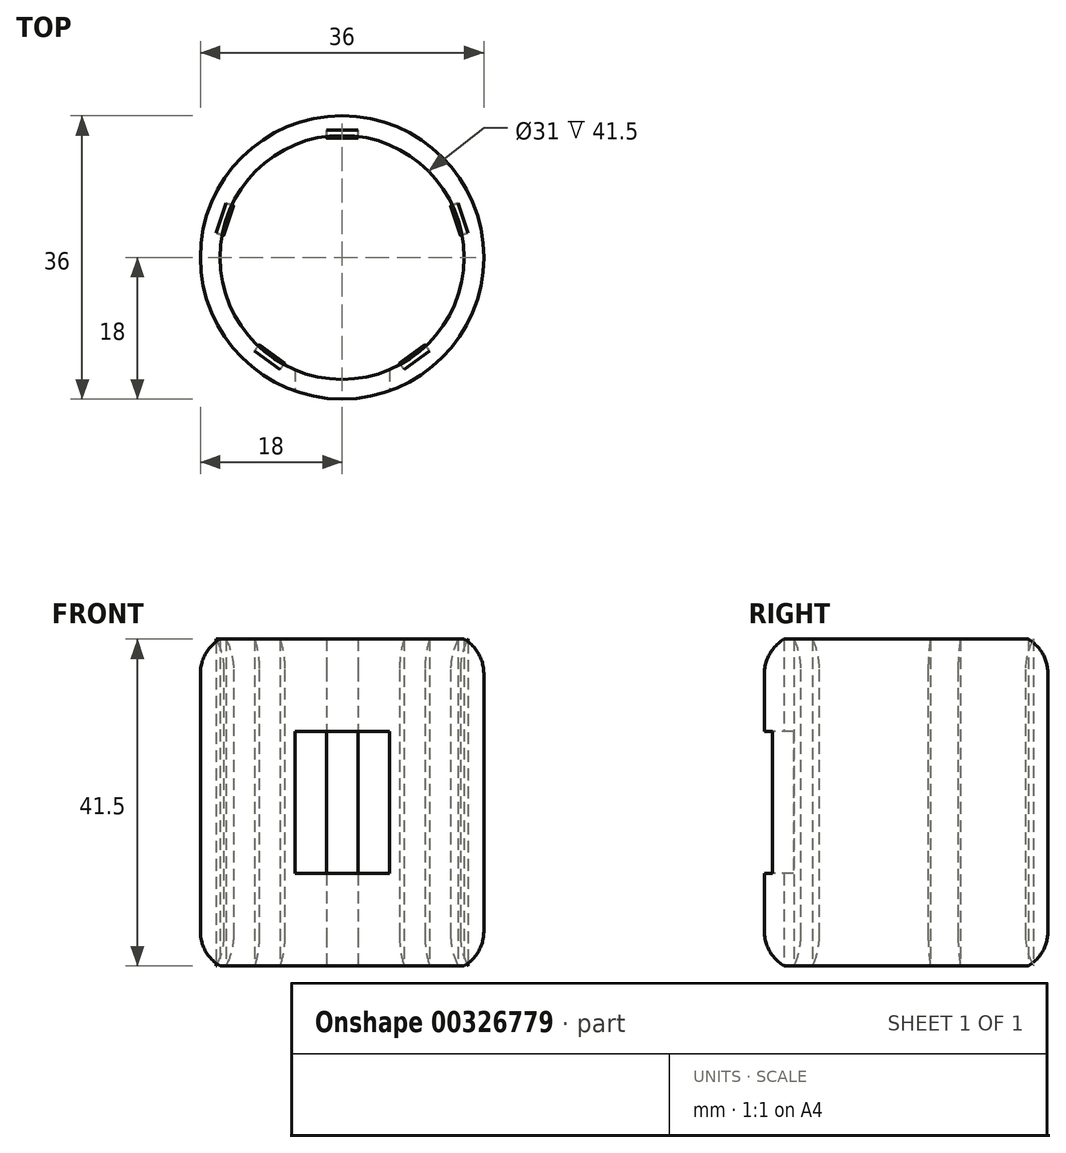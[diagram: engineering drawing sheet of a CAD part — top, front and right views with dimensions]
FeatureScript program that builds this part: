
annotation { "Feature Type Name" : "Feature", "Feature Type Description" : "" }
export const myFeature = defineFeature(function(context is Context, id is Id, definition is map)
    precondition{}
    {
        {
            var Q0;
            Q0=qCreatedBy(makeId("Top.planeOp"),FACE);
            var sketch = newSketch(context, id + "F0", { "sketchPlane" : qUnion([Q0])});
            skCircle(sketch, "E0", {"center": v(0, 0) * mm, "radius": 15.5 * mm});
            skCircle(sketch, "E1.0", {"center": v(0, 0) * mm, "radius": 18 * mm});
            skSolve(sketch);
        }
        {
            var Q0;
            Q0 = qSketchRegion(id + "F0", true);
            extrude(context, id + "F1", {"entities" : qUnion([Q0]), "endBound" : BoundingType.SYMMETRIC, "depth" : 41.5 * mm});
        }
        {
            var Q0;
            Q0=qCreatedBy(makeId("Front.planeOp"),FACE);
            cPlane(context, id + "F2", {"entities" : qUnion([Q0]), "cplaneType" : CPlaneType.OFFSET, "offset" : 16.8 * mm, "width" : 150 * mm, "height" : 150 * mm});
        }
        {
            var Q0;
            Q0=qCreatedBy(id+"F2.planeOp",FACE);
            var sketch = newSketch(context, id + "F3", { "sketchPlane" : qUnion([Q0])});
            skLineSegment(sketch, "E2.bottom", {"start": v(-6, -9) * mm, "end": v(6, -9) * mm});
            skLineSegment(sketch, "E2.top", {"start": v(-6, 9) * mm, "end": v(6, 9) * mm});
            skLineSegment(sketch, "E2.left", {"start": v(-6, -9) * mm, "end": v(-6, 9) * mm});
            skLineSegment(sketch, "E2.right", {"start": v(6, -9) * mm, "end": v(6, 9) * mm});
            skPoint(sketch, "E2.middle", {"position": v(0, 0) * mm});
            skSolve(sketch);
        }
        {
            var Q0;
            Q0 = qSketchRegion(id + "F3", true);
            extrude(context, id + "F4", {"entities" : qUnion([Q0]), "operationType" : NewBodyOperationType.REMOVE, "endBound" : BoundingType.SYMMETRIC, "oppositeDirection" : true, "depth" : 44.13 * mm});
        }
        {
            var Q0;
            Q0=qCreatedBy(makeId("Front.planeOp"),FACE);
            cPlane(context, id + "F5", {"entities" : qUnion([Q0]), "cplaneType" : CPlaneType.OFFSET, "offset" : 16.16 * mm, "oppositeDirection" : true, "width" : 150 * mm, "height" : 150 * mm});
        }
        {
            var Q0;
            Q0=qCreatedBy(id+"F5.planeOp",FACE);
            var sketch = newSketch(context, id + "F6", { "sketchPlane" : qUnion([Q0])});
            skLineSegment(sketch, "E3.bottom", {"start": v(-2, 20.75) * mm, "end": v(2, 20.75) * mm});
            skLineSegment(sketch, "E3.top", {"start": v(-2, -20.75) * mm, "end": v(2, -20.75) * mm});
            skLineSegment(sketch, "E3.left", {"start": v(-2, 20.75) * mm, "end": v(-2, -20.75) * mm});
            skLineSegment(sketch, "E3.right", {"start": v(2, 20.75) * mm, "end": v(2, -20.75) * mm});
            skPoint(sketch, "E3.middle", {"position": v(0, 0) * mm});
            skSolve(sketch);
        }
        {
            var Q0;
            Q0 = qSketchRegion(id + "F6", true);
            extrude(context, id + "F7", {"entities" : qUnion([Q0]), "depth" : 1 * mm});
        }
        {
            var Q0;
            Q0=makeQuery(id+"F7.opExtrude","SWEPT_BODY",BODY,{"disambiguationData":[OSD([sQuery(id+"F6.wireOp",EDGE,"E3.bottom"),sQuery(id+"F6.wireOp",EDGE,"E3.top"),sQuery(id+"F6.wireOp",EDGE,"E3.left"),sQuery(id+"F6.wireOp",EDGE,"E3.right")])]});
            var Q1;
            Q1=makeQuery(id+"F1.opExtrude","SWEPT_FACE",FACE,{"disambiguationData":[OSD([sQuery(id+"F0.wireOp",EDGE,"E0")])]});
            circularPattern(context, id + "F8", {"entities" : qUnion([Q0]), "axis" : qUnion([Q1]), "angle" : 360 * degree, "instanceCount" : 5, "equalSpace" : true});
        }
        {
            var Q0;
            Q0=makeQuery(id+"F7.opExtrude","CAP_EDGE",EDGE,{"disambiguationData":[OSD([sQuery(id+"F6.wireOp",EDGE,"E3.bottom")])],"isStart":false});
            var Q1;
            Q1=makeQuery(id+"F7.opExtrude","CAP_EDGE",EDGE,{"disambiguationData":[OSD([sQuery(id+"F6.wireOp",EDGE,"E3.top")])],"isStart":false});
            var Q2;
            Q2=makeQuery(id+"F8.opPattern","COPY",EDGE,{"derivedFrom":makeQuery(id+"F7.opExtrude","CAP_EDGE",EDGE,{"disambiguationData":[OSD([sQuery(id+"F6.wireOp",EDGE,"E3.bottom")])],"isStart":false}),"instanceName":"1"});
            var Q3;
            Q3=makeQuery(id+"F8.opPattern","COPY",EDGE,{"derivedFrom":makeQuery(id+"F7.opExtrude","CAP_EDGE",EDGE,{"disambiguationData":[OSD([sQuery(id+"F6.wireOp",EDGE,"E3.bottom")])],"isStart":false}),"instanceName":"2"});
            var Q4;
            Q4=makeQuery(id+"F8.opPattern","COPY",EDGE,{"derivedFrom":makeQuery(id+"F7.opExtrude","CAP_EDGE",EDGE,{"disambiguationData":[OSD([sQuery(id+"F6.wireOp",EDGE,"E3.top")])],"isStart":false}),"instanceName":"2"});
            var Q5;
            Q5=makeQuery(id+"F8.opPattern","COPY",EDGE,{"derivedFrom":makeQuery(id+"F7.opExtrude","CAP_EDGE",EDGE,{"disambiguationData":[OSD([sQuery(id+"F6.wireOp",EDGE,"E3.top")])],"isStart":false}),"instanceName":"1"});
            var Q6;
            Q6=makeQuery(id+"F8.opPattern","COPY",EDGE,{"derivedFrom":makeQuery(id+"F7.opExtrude","CAP_EDGE",EDGE,{"disambiguationData":[OSD([sQuery(id+"F6.wireOp",EDGE,"E3.bottom")])],"isStart":false}),"instanceName":"4"});
            var Q7;
            Q7=makeQuery(id+"F8.opPattern","COPY",EDGE,{"derivedFrom":makeQuery(id+"F7.opExtrude","CAP_EDGE",EDGE,{"disambiguationData":[OSD([sQuery(id+"F6.wireOp",EDGE,"E3.bottom")])],"isStart":false}),"instanceName":"3"});
            var Q8;
            Q8=makeQuery(id+"F8.opPattern","COPY",EDGE,{"derivedFrom":makeQuery(id+"F7.opExtrude","CAP_EDGE",EDGE,{"disambiguationData":[OSD([sQuery(id+"F6.wireOp",EDGE,"E3.top")])],"isStart":false}),"instanceName":"3"});
            var Q9;
            Q9=makeQuery(id+"F8.opPattern","COPY",EDGE,{"derivedFrom":makeQuery(id+"F7.opExtrude","CAP_EDGE",EDGE,{"disambiguationData":[OSD([sQuery(id+"F6.wireOp",EDGE,"E3.top")])],"isStart":false}),"instanceName":"4"});
            fillet(context, id + "F9", {"entities" : qUnion([Q0, Q1, Q2, Q3, Q4, Q5, Q6, Q7, Q8, Q9]), "radius" : 8 * mm, "tangentPropagation" : true, "allowEdgeOverflow" : false});
        }
        {
            var Q0;
            Q0=makeQuery(id+"F1.opExtrude","CAP_EDGE",EDGE,{"disambiguationData":[OSD([sQuery(id+"F0.wireOp",EDGE,"E1.0")])],"isStart":false});
            var Q1;
            Q1=makeQuery(id+"F1.opExtrude","CAP_EDGE",EDGE,{"disambiguationData":[OSD([sQuery(id+"F0.wireOp",EDGE,"E1.0")])],"isStart":true});
            fillet(context, id + "F10", {"entities" : qUnion([Q0, Q1]), "radius" : 5 * mm, "tangentPropagation" : true, "allowEdgeOverflow" : false});
        }
    });
